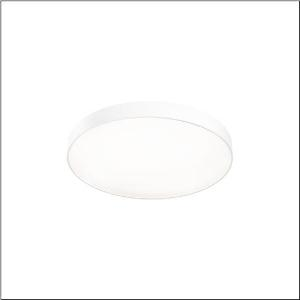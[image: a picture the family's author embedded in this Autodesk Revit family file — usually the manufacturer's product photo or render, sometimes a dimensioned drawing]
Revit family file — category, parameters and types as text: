
# Revit family: round_21_m_51mr36gd0421w
name_source: partatom
category: Lighting Fixtures
units: mm (PartAtom-declared; Revit-internal decimal feet)

## family parameters
Cut with Voids When Loaded = No
Host = Face
Light Source = No
Part Type = Normal
Room Calculation Point = No
Round Connector Dimension = Use Diameter
Shared = No

## types (1)
- Round 21 M (1 x LED, 7870 lm, 54.6 W, 4000K)
    Apparent Load = 55 VA
    CIE Flux Codes = 49 80 96 85 100
    Color Rendering = 80
    Color Temperature = 4000K
    Default Elevation = 1800 mm
    Description = Round 21 M, wall and ceiling luminaire, primary optical cover: cover, of PMMA, opal, light emission: direct/indirect distribution, primary light characteristic: symmetric, installation type: suspended mounting, surface-mounted, LED, rated luminous flux: 7.870lm, luminous efficacy: 144lm/W, light colour: 840, colour temperature: 4000K, with terminal, 5-pole, mains connection: 230V, AC, 50/60Hz, rated input power: 54.6W, housing, of aluminium, coated, white, diameter: 600mm, height: 62mm, protection rating (complete): IP40, insulation class (complete): insulation class I (protective earthing), certification: CE, impact resistance: IK04, permissible operating ambient temperature: -10..+35°C, packaging unit: 1 piece
    Height = 87 mm
    Lamp = 1 x LED
    Lamp Light Flux = 7870 lm
    Lamp Power = 54.6 W
    Lamp count = 1
    Length = 600 mm
    Luminous efficacy = 144 lm/W
    Manufacturer = Siteco
    ModVariant = No
    Model = 51MR36GD0421W
    Mounting Place = Ceiling
    Mounting Type = Surface mounted
    Number of Poles = 1
    OnlyDefault = Yes
    Power Factor = 1
    Product Name = Round 21 M
    Product group = wall and ceiling luminaire
    ProductGroupID = 303
    Protection Class = Protection class I
    Protection Degree = IP 40
    RLX_Detail_Level = 1
    RLX_Emergency_Light_Flux = 0 lm
    RLX_Emergency_Type = 0
    RLX_Emergency_Type_DB = No
    RlxData = <blob elided: 12097 chars, md5=05c95f67>
    Socket = socket
    Standby Power = 0 W
    System Light Flux = 7870 lm
    System Power = 55 W
    Type Comments = Product without accessories
    Type Image = l_1258330.jpg
    URL = http://relux.com
    VarID = ---
    Voltage = 0 V
    Weight = 0.00 kg
    Width = 0 mm  [stored 0 ft]

note: [stored X ft] marks values corroborated as IEEE doubles in the binary element streams (Revit-internal decimal feet)

## geometry (parser evidence)
native form markers: Sweep x11
no freeform markers — native parametric forms only
